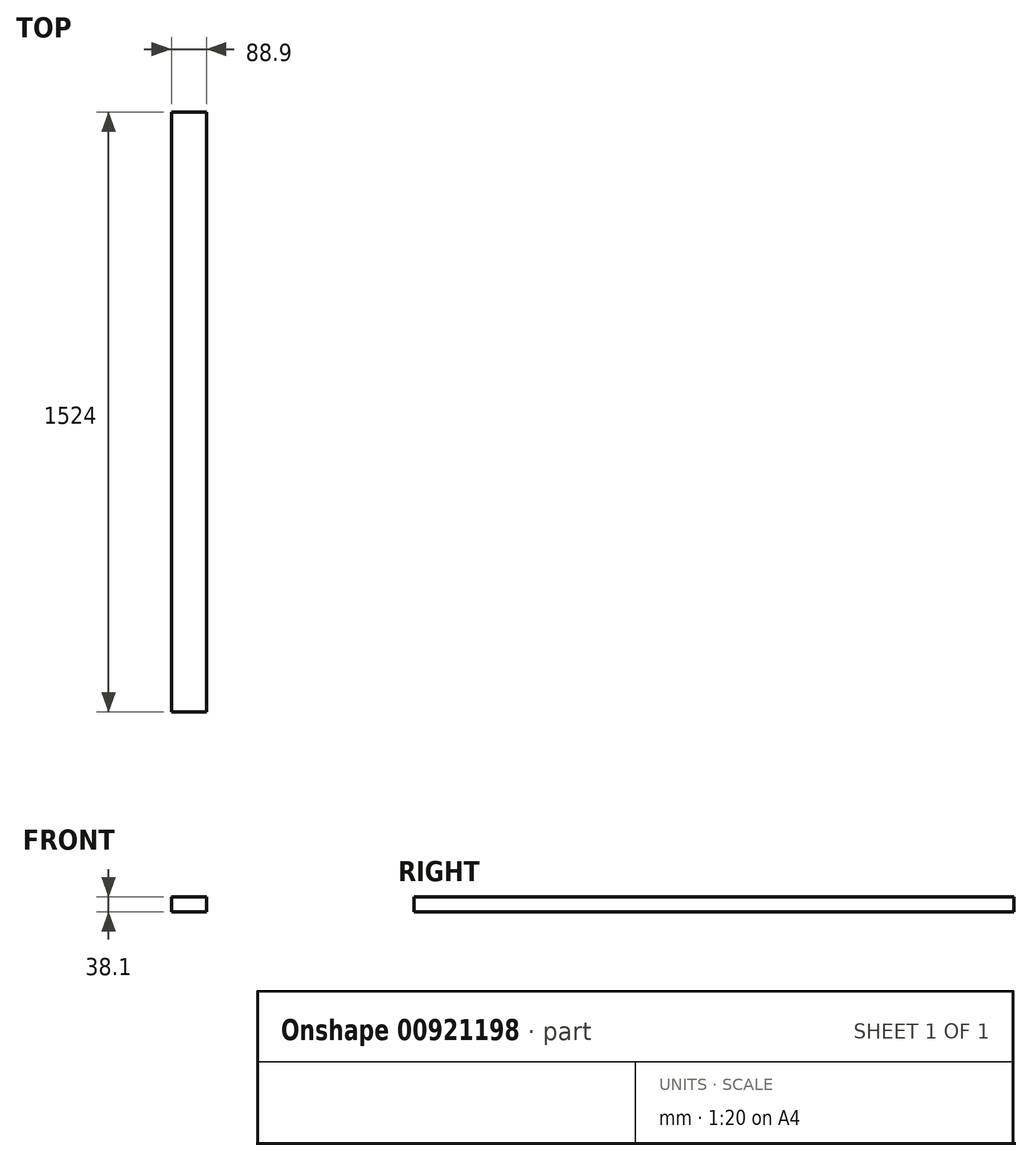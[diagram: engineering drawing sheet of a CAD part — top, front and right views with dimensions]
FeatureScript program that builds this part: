
annotation { "Feature Type Name" : "Feature", "Feature Type Description" : "" }
export const myFeature = defineFeature(function(context is Context, id is Id, definition is map)
    precondition{}
    {
        {
            var Q0;
            Q0=qCreatedBy(makeId("Front.planeOp"),FACE);
            var sketch = newSketch(context, id + "F0", { "sketchPlane" : qUnion([Q0])});
            skLineSegment(sketch, "E0.bottom", {"start": v(0, 0) * mm, "end": v(88.9, 0) * mm});
            skLineSegment(sketch, "E0.top", {"start": v(0, 38.1) * mm, "end": v(88.9, 38.1) * mm});
            skLineSegment(sketch, "E0.left", {"start": v(0, 0) * mm, "end": v(0, 38.1) * mm});
            skLineSegment(sketch, "E0.right", {"start": v(88.9, 0) * mm, "end": v(88.9, 38.1) * mm});
            skSolve(sketch);
        }
        {
            var Q0;
            Q0 = qSketchRegion(id + "F0", true);
            extrude(context, id + "F1", {"entities" : qUnion([Q0]), "flatOperationType" : FlatOperationType.REMOVE, "depth" : 1524 * mm, "offsetDistance" : 25.4 * mm, "domain" : OperationDomain.MODEL});
        }
    });
